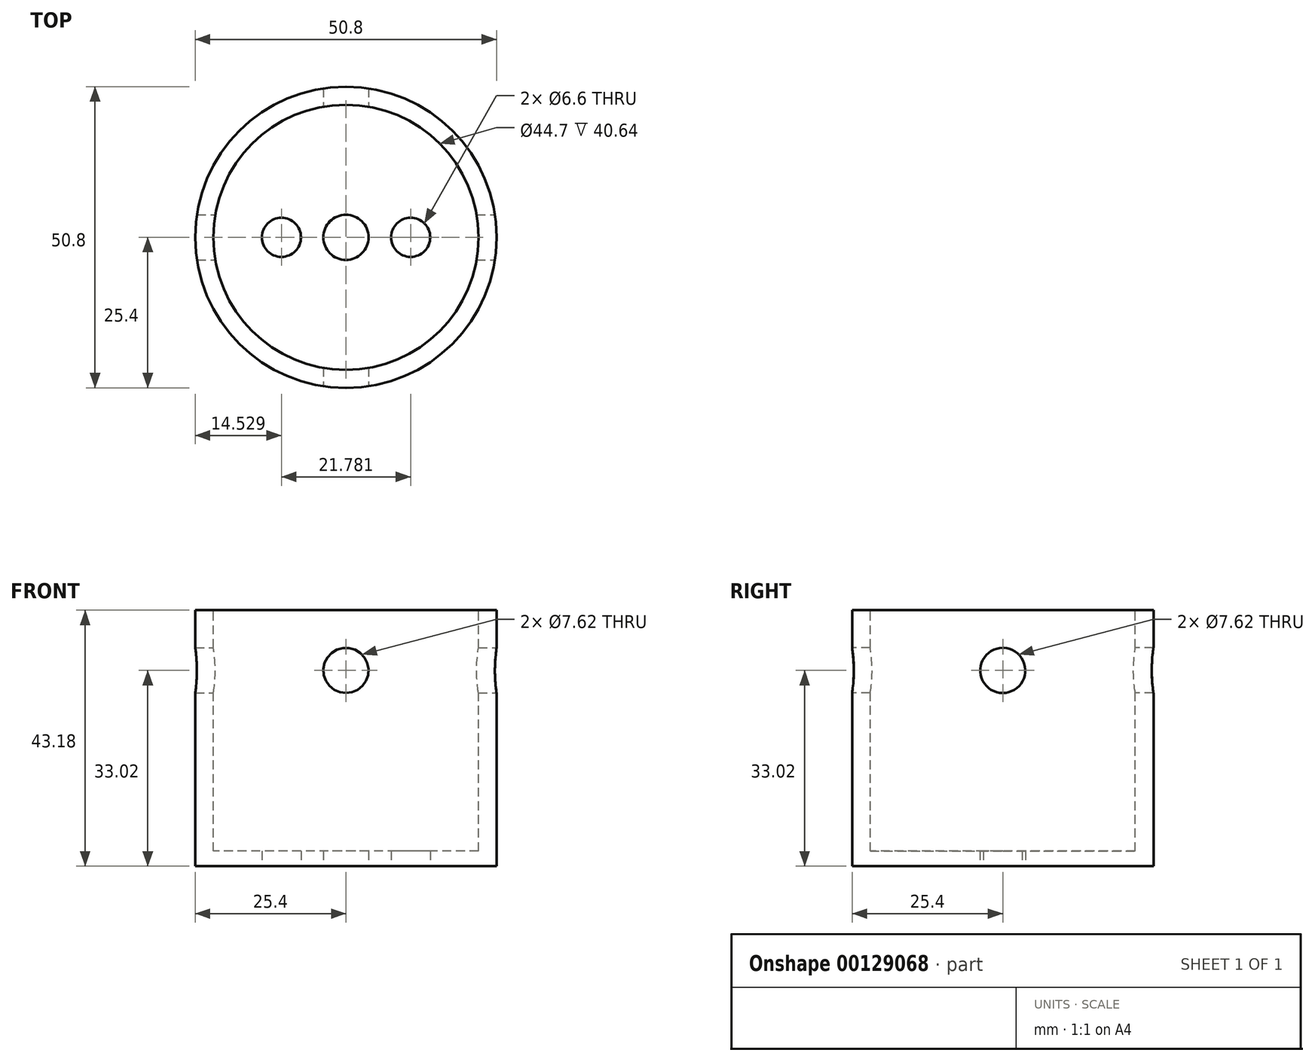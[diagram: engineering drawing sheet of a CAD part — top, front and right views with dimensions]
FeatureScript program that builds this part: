
annotation { "Feature Type Name" : "Feature", "Feature Type Description" : "" }
export const myFeature = defineFeature(function(context is Context, id is Id, definition is map)
    precondition{}
    {
        {
            var Q0;
            Q0=qCreatedBy(makeId("Top.planeOp"),FACE);
            var sketch = newSketch(context, id + "F0", { "sketchPlane" : qUnion([Q0])});
            skCircle(sketch, "E0", {"center": v(0, 0) * mm, "radius": 25.4 * mm});
            skSolve(sketch);
        }
        {
            var Q0;
            Q0 = qSketchRegion(id + "F0", true);
            extrude(context, id + "F1", {"entities" : qUnion([Q0]), "oppositeDirection" : true, "depth" : 43.18 * mm});
        }
        {
            var Q0;
            Q0=makeQuery(id+"F1.opExtrude","CAP_FACE",FACE,{"disambiguationData":[OSD([sQuery(id+"F0.wireOp",EDGE,"E0")])],"isStart":false});
            var sketch = newSketch(context, id + "F2", { "sketchPlane" : qUnion([Q0])});
            skCircle(sketch, "E1", {"center": v(0, 0) * mm, "radius": 3.8 * mm});
            skSolve(sketch);
        }
        {
            var Q0;
            Q0 = qSketchRegion(id + "F2", true);
            extrude(context, id + "F3", {"entities" : qUnion([Q0]), "operationType" : NewBodyOperationType.REMOVE, "endBound" : BoundingType.THROUGH_ALL, "oppositeDirection" : true, "depth" : 38.1 * mm});
        }
        {
            var Q0;
            Q0=qCreatedBy(makeId("Right.planeOp"),FACE);
            var sketch = newSketch(context, id + "F4", { "sketchPlane" : qUnion([Q0])});
            skLineSegment(sketch, "E2", {"start": v(0, 0) * mm, "end": v(0, -74.59) * mm, "construction": true});
            skCircle(sketch, "E3", {"center": v(0, -10.16) * mm, "radius": 3.81 * mm});
            skSolve(sketch);
        }
        {
            var Q0;
            Q0 = qSketchRegion(id + "F4", true);
            extrude(context, id + "F5", {"entities" : qUnion([Q0]), "operationType" : NewBodyOperationType.REMOVE, "endBound" : BoundingType.THROUGH_ALL, "oppositeDirection" : true, "depth" : 25.4 * mm, "hasSecondDirection" : true, "secondDirectionBound" : BoundingType.THROUGH_ALL, "secondDirectionOppositeDirection" : false, "secondDirectionDepth" : 25.4 * mm});
        }
        {
            var Q0;
            Q0=qCreatedBy(makeId("Front.planeOp"),FACE);
            var sketch = newSketch(context, id + "F6", { "sketchPlane" : qUnion([Q0])});
            skLineSegment(sketch, "E4", {"start": v(0, 0) * mm, "end": v(0, -36.04) * mm, "construction": true});
            skCircle(sketch, "E5", {"center": v(0, -10.16) * mm, "radius": 3.81 * mm});
            skSolve(sketch);
        }
        {
            var Q0;
            Q0 = qSketchRegion(id + "F6", true);
            extrude(context, id + "F7", {"entities" : qUnion([Q0]), "operationType" : NewBodyOperationType.REMOVE, "endBound" : BoundingType.THROUGH_ALL, "oppositeDirection" : true, "depth" : 25.4 * mm, "hasSecondDirection" : true, "secondDirectionBound" : BoundingType.THROUGH_ALL, "secondDirectionOppositeDirection" : false, "secondDirectionDepth" : 25.4 * mm});
        }
        {
            var Q0;
            Q0=makeQuery(id+"F1.opExtrude","CAP_FACE",FACE,{"disambiguationData":[OSD([sQuery(id+"F0.wireOp",EDGE,"E0")])],"isStart":false});
            var sketch = newSketch(context, id + "F8", { "sketchPlane" : qUnion([Q0])});
            skCircle(sketch, "E6", {"center": v(10.9, 0) * mm, "radius": 3.3 * mm});
            skCircle(sketch, "E7", {"center": v(-10.87, 0) * mm, "radius": 3.3 * mm});
            skSolve(sketch);
        }
        {
            var Q0;
            Q0 = qSketchRegion(id + "F8", true);
            extrude(context, id + "F9", {"entities" : qUnion([Q0]), "operationType" : NewBodyOperationType.REMOVE, "endBound" : BoundingType.THROUGH_ALL, "oppositeDirection" : true, "depth" : 31.86 * mm});
        }
        {
            var Q0;
            Q0=makeQuery(id+"F1.opExtrude","CAP_FACE",FACE,{"disambiguationData":[OSD([sQuery(id+"F0.wireOp",EDGE,"E0")])],"isStart":true});
            var sketch = newSketch(context, id + "F10", { "sketchPlane" : qUnion([Q0])});
            skCircle(sketch, "E8", {"center": v(0, 0) * mm, "radius": 22.35 * mm});
            skSolve(sketch);
        }
        {
            var Q0;
            Q0 = qSketchRegion(id + "F10", true);
            extrude(context, id + "F11", {"entities" : qUnion([Q0]), "operationType" : NewBodyOperationType.REMOVE, "oppositeDirection" : true, "depth" : 40.64 * mm});
        }
    });
